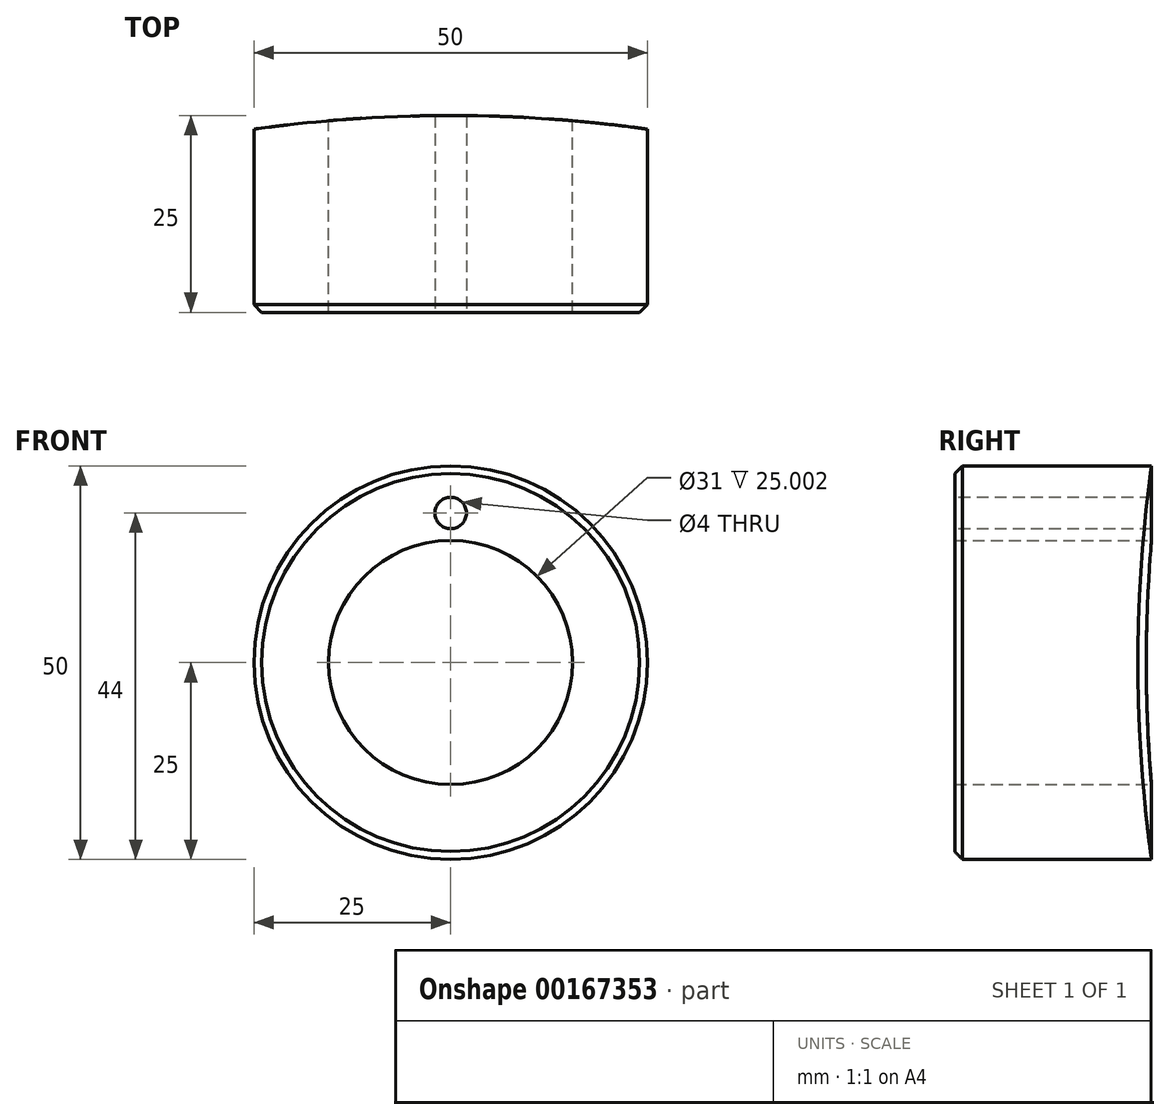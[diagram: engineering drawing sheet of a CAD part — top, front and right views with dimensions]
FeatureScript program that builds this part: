
annotation { "Feature Type Name" : "Feature", "Feature Type Description" : "" }
export const myFeature = defineFeature(function(context is Context, id is Id, definition is map)
    precondition{}
    {
        {
            var Q0;
            Q0=qCreatedBy(makeId("Front.planeOp"),FACE);
            var sketch = newSketch(context, id + "F0", { "sketchPlane" : qUnion([Q0])});
            skCircle(sketch, "E0", {"center": v(0, 0) * mm, "radius": 15.5 * mm});
            skCircle(sketch, "E1", {"center": v(0, 0) * mm, "radius": 25 * mm});
            skSolve(sketch);
        }
        {
            var Q0;
            Q0=makeQuery(id+"F0.imprint","IMPRINT",FACE,{"disambiguationData":[TD([[makeQuery(id+"F0.imprint","IMPRINT",EDGE,{"derivedFrom":sQuery(id+"F0.wireOp",EDGE,"E0")}),-1.0]])]});
            extrude(context, id + "F1", {"entities" : qUnion([Q0]), "depth" : 25 * mm});
        }
        {
            var Q0;
            Q0=qCreatedBy(makeId("Top.planeOp"),FACE);
            var sketch = newSketch(context, id + "F2", { "sketchPlane" : qUnion([Q0])});
            skArc(sketch, "E2", {"start": v(25, -1.73) * mm, "mid": v(0, 0) * mm, "end": v(-25, -1.73) * mm});
            skLineSegment(sketch, "E3", {"start": v(-25, -1.73) * mm, "end": v(-25, 5) * mm});
            skLineSegment(sketch, "E4", {"start": v(-25, 5) * mm, "end": v(25, 5) * mm});
            skLineSegment(sketch, "E5", {"start": v(25, 5) * mm, "end": v(25, -1.73) * mm});
            skSolve(sketch);
        }
        {
            var Q0;
            Q0=makeQuery(id+"F2.imprint","IMPRINT",FACE,{"disambiguationData":[TD([[makeQuery(id+"F2.imprint","IMPRINT",EDGE,{"derivedFrom":sQuery(id+"F2.wireOp",EDGE,"E2")}),-1.0]])]});
            extrude(context, id + "F3", {"entities" : qUnion([Q0]), "operationType" : NewBodyOperationType.REMOVE, "endBound" : BoundingType.THROUGH_ALL, "oppositeDirection" : true, "depth" : 25 * mm, "hasSecondDirection" : true, "secondDirectionBound" : SecondDirectionBoundingType.THROUGH_ALL, "secondDirectionOppositeDirection" : false, "secondDirectionDepth" : 25 * mm});
        }
        {
            var Q0;
            Q0=makeQuery(id+"F1.opExtrude","CAP_EDGE",EDGE,{"disambiguationData":[OSD([sQuery(id+"F0.wireOp",EDGE,"E1")])],"isStart":false});
            chamfer(context, id + "F4", {"entities" : qUnion([Q0]), "width" : 1 * mm, "tangentPropagation" : true});
        }
        {
            var Q0;
            Q0=makeQuery(id+"F1.opExtrude","CAP_FACE",FACE,{"disambiguationData":[OSD([sQuery(id+"F0.wireOp",EDGE,"E0"),sQuery(id+"F0.wireOp",EDGE,"E1")])],"isStart":false});
            var sketch = newSketch(context, id + "F5", { "sketchPlane" : qUnion([Q0])});
            skPoint(sketch, "E6", {"position": v(0, 19) * mm});
            skSolve(sketch);
        }
        {
            var Q0;
            Q0=sQuery(id+"F5.wireOp",VERTEX,"E6");
            var Q1;
            Q1=makeQuery(id+"F1.opExtrude","SWEPT_BODY",BODY,{"disambiguationData":[OSD([sQuery(id+"F0.wireOp",EDGE,"E0"),sQuery(id+"F0.wireOp",EDGE,"E1")])]});
            hole(context, id + "F6", {"style" : HoleStyle.SIMPLE, "endStyle" : HoleEndStyle.THROUGH, "holeDiameter" : 4 * mm, "locations" : qUnion([Q0]), "scope" : qUnion([Q1]), "isTappedThrough" : true});
        }
    });
